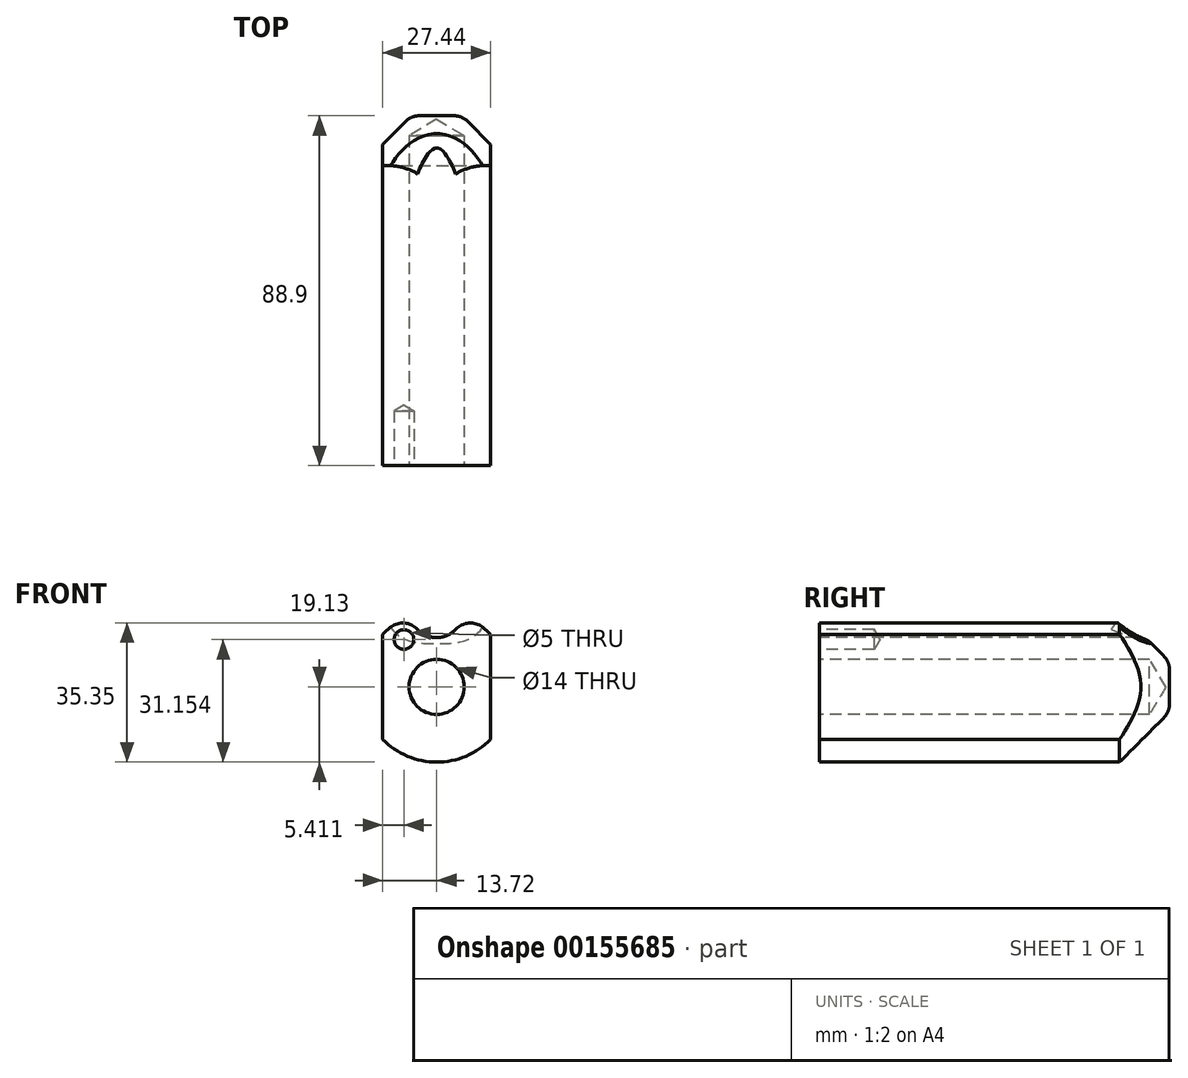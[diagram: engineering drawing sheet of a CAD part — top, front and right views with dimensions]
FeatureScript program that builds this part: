
annotation { "Feature Type Name" : "Feature", "Feature Type Description" : "" }
export const myFeature = defineFeature(function(context is Context, id is Id, definition is map)
    precondition{}
    {
        {
            var Q0;
            Q0=qCreatedBy(makeId("Front.planeOp"),FACE);
            var sketch = newSketch(context, id + "F0", { "sketchPlane" : qUnion([Q0])});
            skArc(sketch, "E0", {"start": v(-6.52, 17.98) * mm, "mid": v(-10.38, 16.06) * mm, "end": v(-13.72, 13.33) * mm});
            skCircle(sketch, "E1", {"center": v(0, 0) * mm, "radius": 6.5 * mm});
            skLineSegment(sketch, "E2", {"start": v(0, 6.5) * mm, "end": v(0, 12.5) * mm, "construction": true});
            skArc(sketch, "E3", {"start": v(-6.52, 17.98) * mm, "mid": v(0, 12.5) * mm, "end": v(6.52, 17.98) * mm});
            skCircle(sketch, "E4", {"center": v(-8.3, 12.02) * mm, "radius": 2.3 * mm});
            skLineSegment(sketch, "E5", {"start": v(-13.72, 13.33) * mm, "end": v(-13.72, -13.33) * mm});
            skLineSegment(sketch, "E6", {"start": v(13.72, 13.33) * mm, "end": v(13.72, -13.33) * mm});
            skArc(sketch, "E7.trimOffspring", {"start": v(-13.72, -13.33) * mm, "mid": v(0, -19.12) * mm, "end": v(13.72, -13.33) * mm});
            skArc(sketch, "E8.trimOffspring", {"start": v(13.72, 13.33) * mm, "mid": v(10.38, 16.06) * mm, "end": v(6.52, 17.98) * mm});
            skLineSegment(sketch, "E9", {"start": v(0, 0) * mm, "end": v(13.72, 0) * mm, "construction": true});
            skLineSegment(sketch, "E10", {"start": v(0, 0) * mm, "end": v(-13.72, 0) * mm, "construction": true});
            skSolve(sketch);
        }
        {
            var Q0;
            Q0 = qSketchRegion(id + "F0", true);
            var Q1;
            Q1=makeQuery(id+"F0.imprint","IMPRINT",FACE,{"disambiguationData":[TD([[makeQuery(id+"F0.imprint","IMPRINT",EDGE,{"derivedFrom":sQuery(id+"F0.wireOp",EDGE,"E1")}),1.0]])]});
            var Q2;
            Q2=makeQuery(id+"F0.imprint","IMPRINT",FACE,{"disambiguationData":[TD([[makeQuery(id+"F0.imprint","IMPRINT",EDGE,{"derivedFrom":sQuery(id+"F0.wireOp",EDGE,"E4")}),1.0]])]});
            extrude(context, id + "F1", {"entities" : qUnion([Q0, Q1, Q2]), "oppositeDirection" : true, "depth" : 88.9 * mm});
        }
        {
            var Q0;
            Q0=sQuery(id+"F0.wireOp",VERTEX,"E4.center");
            var Q1;
            Q1=makeQuery(id+"F1.opExtrude","SWEPT_BODY",BODY,{"disambiguationData":[OSD([sQuery(id+"F0.wireOp",EDGE,"E0"),sQuery(id+"F0.wireOp",EDGE,"E3"),sQuery(id+"F0.wireOp",EDGE,"E5"),sQuery(id+"F0.wireOp",EDGE,"E6"),sQuery(id+"F0.wireOp",EDGE,"E7.trimOffspring"),sQuery(id+"F0.wireOp",EDGE,"E8.trimOffspring")])]});
            hole(context, id + "F2", {"style" : HoleStyle.SIMPLE, "endStyle" : HoleEndStyle.BLIND, "holeDiameter" : 5 * mm, "holeDepth" : 13.9 * mm, "startFromSketch" : true, "locations" : qUnion([Q0]), "scope" : qUnion([Q1])});
        }
        {
            var Q0;
            Q0=sQuery(id+"F0.wireOp",VERTEX,"E8.trimOffspring.center");
            var Q1;
            Q1=makeQuery(id+"F1.opExtrude","SWEPT_BODY",BODY,{"disambiguationData":[OSD([sQuery(id+"F0.wireOp",EDGE,"E0"),sQuery(id+"F0.wireOp",EDGE,"E3"),sQuery(id+"F0.wireOp",EDGE,"E5"),sQuery(id+"F0.wireOp",EDGE,"E6"),sQuery(id+"F0.wireOp",EDGE,"E7.trimOffspring"),sQuery(id+"F0.wireOp",EDGE,"E8.trimOffspring")])]});
            hole(context, id + "F3", {"style" : HoleStyle.SIMPLE, "endStyle" : HoleEndStyle.BLIND, "holeDiameter" : 14 * mm, "holeDepth" : 83.82 * mm, "startFromSketch" : true, "locations" : qUnion([Q0]), "scope" : qUnion([Q1])});
        }
        {
            var Q0;
            Q0=makeQuery(id+"F1.opExtrude","CAP_EDGE",EDGE,{"disambiguationData":[OSD([sQuery(id+"F0.wireOp",EDGE,"E6")])],"isStart":false});
            var Q1;
            Q1=makeQuery(id+"F1.opExtrude","CAP_EDGE",EDGE,{"disambiguationData":[OSD([sQuery(id+"F0.wireOp",EDGE,"E5")])],"isStart":false});
            var Q2;
            Q2=makeQuery(id+"F1.opExtrude","CAP_EDGE",EDGE,{"disambiguationData":[OSD([sQuery(id+"F0.wireOp",EDGE,"E0")])],"isStart":false});
            var Q3;
            Q3=makeQuery(id+"F1.opExtrude","CAP_EDGE",EDGE,{"disambiguationData":[OSD([sQuery(id+"F0.wireOp",EDGE,"E8.trimOffspring")])],"isStart":false});
            var Q4;
            Q4=makeQuery(id+"F1.opExtrude","CAP_EDGE",EDGE,{"disambiguationData":[OSD([sQuery(id+"F0.wireOp",EDGE,"E3")])],"isStart":false});
            chamfer(context, id + "F4", {"entities" : qUnion([Q0, Q1, Q2, Q3, Q4]), "width" : 5.08 * mm, "tangentPropagation" : true});
        }
        {
            var Q0;
            Q0=makeQuery(id+"F1.opExtrude","CAP_EDGE",EDGE,{"disambiguationData":[OSD([sQuery(id+"F0.wireOp",EDGE,"E7.trimOffspring")])],"isStart":false});
            chamfer(context, id + "F5", {"entities" : qUnion([Q0]), "width" : 12.7 * mm, "tangentPropagation" : true});
        }
        {
            var Q0;
            Q0=makeQuery(id+"F5.opChamfer","BLEND_EDGE",EDGE,{"blendedFrom":[makeQuery(id+"F1.opExtrude","CAP_EDGE",EDGE,{"disambiguationData":[OSD([sQuery(id+"F0.wireOp",EDGE,"E7.trimOffspring")])],"isStart":false}),makeQuery(id+"F1.opExtrude","SWEPT_FACE",FACE,{"disambiguationData":[OSD([sQuery(id+"F0.wireOp",EDGE,"E3")])]})],"blendedInto":[makeQuery(id+"F1.opExtrude","SWEPT_FACE",FACE,{"disambiguationData":[OSD([sQuery(id+"F0.wireOp",EDGE,"E3")])]})]});
            var Q1;
            Q1=makeQuery(id+"F1.opExtrude","SWEPT_EDGE",EDGE,{"disambiguationData":[OSD([sQuery(id+"F0.wireOp",EDGE,"E0"),sQuery(id+"F0.wireOp",EDGE,"E3")])]});
            var Q2;
            Q2=makeQuery(id+"F1.opExtrude","SWEPT_EDGE",EDGE,{"disambiguationData":[OSD([sQuery(id+"F0.wireOp",EDGE,"E3"),sQuery(id+"F0.wireOp",EDGE,"E8.trimOffspring")])]});
            var Q3;
            {var subQ0=sQuery(id+"F0.wireOp",EDGE,"E7.trimOffspring");Q3=makeQuery(id+"F5.opChamfer","BLEND_EDGE",EDGE,{"blendedFrom":[makeQuery(id+"F1.opExtrude","CAP_EDGE",EDGE,{"disambiguationData":[OSD([subQ0])],"isStart":false}),makeQuery(id+"F1.opExtrude","CAP_FACE",FACE,{"disambiguationData":[OSD([sQuery(id+"F0.wireOp",EDGE,"E0"),sQuery(id+"F0.wireOp",EDGE,"E3"),sQuery(id+"F0.wireOp",EDGE,"E5"),sQuery(id+"F0.wireOp",EDGE,"E6"),subQ0,sQuery(id+"F0.wireOp",EDGE,"E8.trimOffspring")])],"isStart":false})],"blendedInto":[makeQuery(id+"F1.opExtrude","CAP_FACE",FACE,{"disambiguationData":[OSD([sQuery(id+"F0.wireOp",EDGE,"E0"),sQuery(id+"F0.wireOp",EDGE,"E3"),sQuery(id+"F0.wireOp",EDGE,"E5"),sQuery(id+"F0.wireOp",EDGE,"E6"),subQ0,sQuery(id+"F0.wireOp",EDGE,"E8.trimOffspring")])],"isStart":false})]});}
            var Q4;
            Q4=makeQuery(id+"F3.hole-0.boolean.opBoolean","COPY",EDGE,{"derivedFrom":makeQuery(id+"F3.hole-0.opRevolve","SWEPT_EDGE",EDGE,{"disambiguationData":[OSD([sQuery(id+"F3.hole-0.sketch.wireOp",EDGE,"core_line_2"),sQuery(id+"F3.hole-0.sketch.wireOp",EDGE,"core_line_3")])]})});
            fillet(context, id + "F6", {"entities" : qUnion([Q0, Q1, Q2, Q3, Q4]), "radius" : 5.08 * mm, "tangentPropagation" : true, "allowEdgeOverflow" : false});
        }
    });
